# Revit family: LOROWERK 00672-150X
name_source: partatom
category: Pipe Fittings
revit_build: Autodesk Revit 2017 (Build: 20160225_1515(x64)
units: mm (PartAtom-declared; Revit-internal decimal feet)

## family parameters
Always vertical = Yes
Cut with Voids When Loaded = No
Part Type = Union
Round Connector Dimension = Use Diameter
Shared = No
Work Plane-Based = No

## types (1)
- LOROWERK 00672-150X
    BIM = https://media.stage.bim.site
    Benennung = LORO-X Anschlussstück an KA-HT-Muffe 200/LX 150
    Brandschutzklasse = B1 nach DIN 4102
    CONNECTOR0_DIAMETER_dZ_0r = 150 mm
    CONNECTOR0_dZ_00 = 235 mm
    CONNECTOR0_dZ_01 = 320 mm
    CONNECTOR0_ref_dZ = 235 mm
    CONNECTOR1_DIAMETER_dZ_0r = 200 mm
    CONNECTOR1_dZ_01 = 125 mm
    CONNECTOR1_ref_dZ = 125 mm
    DATANORM = 00672.150X
    Description = LORO-X Stahlabflussrohre
    GTIN = 4038088028124
    HAN = 00672.150X
    Index = 11
    Ist System = No
    Ist Zubehör = No
    Manufacturer = LOROWERK K.H. Vahlbrauk GmbH & Co. KG
    Nenndruck = 0.5
    Nenndrucksystem = PN
    Nennweitensystem = DN
    Normen/Regeln/Zulassungen = DVGW für Trinkwasser
    Produktbezeichnung = LORO-X Stahlabflussrohre
    Produktkennung = Formstück
    Produktname = Anschlussstücke von LORO-X Rohr an Kunststoffabflussrohrmuffen (KA)
    Produktvideo = https://media.stage.bim.site
    Querschnittsform = rund
    Type Name = Anschlussstücke von LORO-X Rohr an Kunststoffabflussrohrmuffen (KA)
    VDIBSN = 020001???001001???00100100000100300700000000000170000000000000000011
    Verbindungsart I = Pressen
    Verbindungsart II = axial pressen
    Verlegeart = unter Putz
    max. zul. Dauer-Betriebstemperatur [K] = 95

## geometry (parser evidence)
native form markers: Blend x2, Sweep x3
no freeform markers — native parametric forms only
